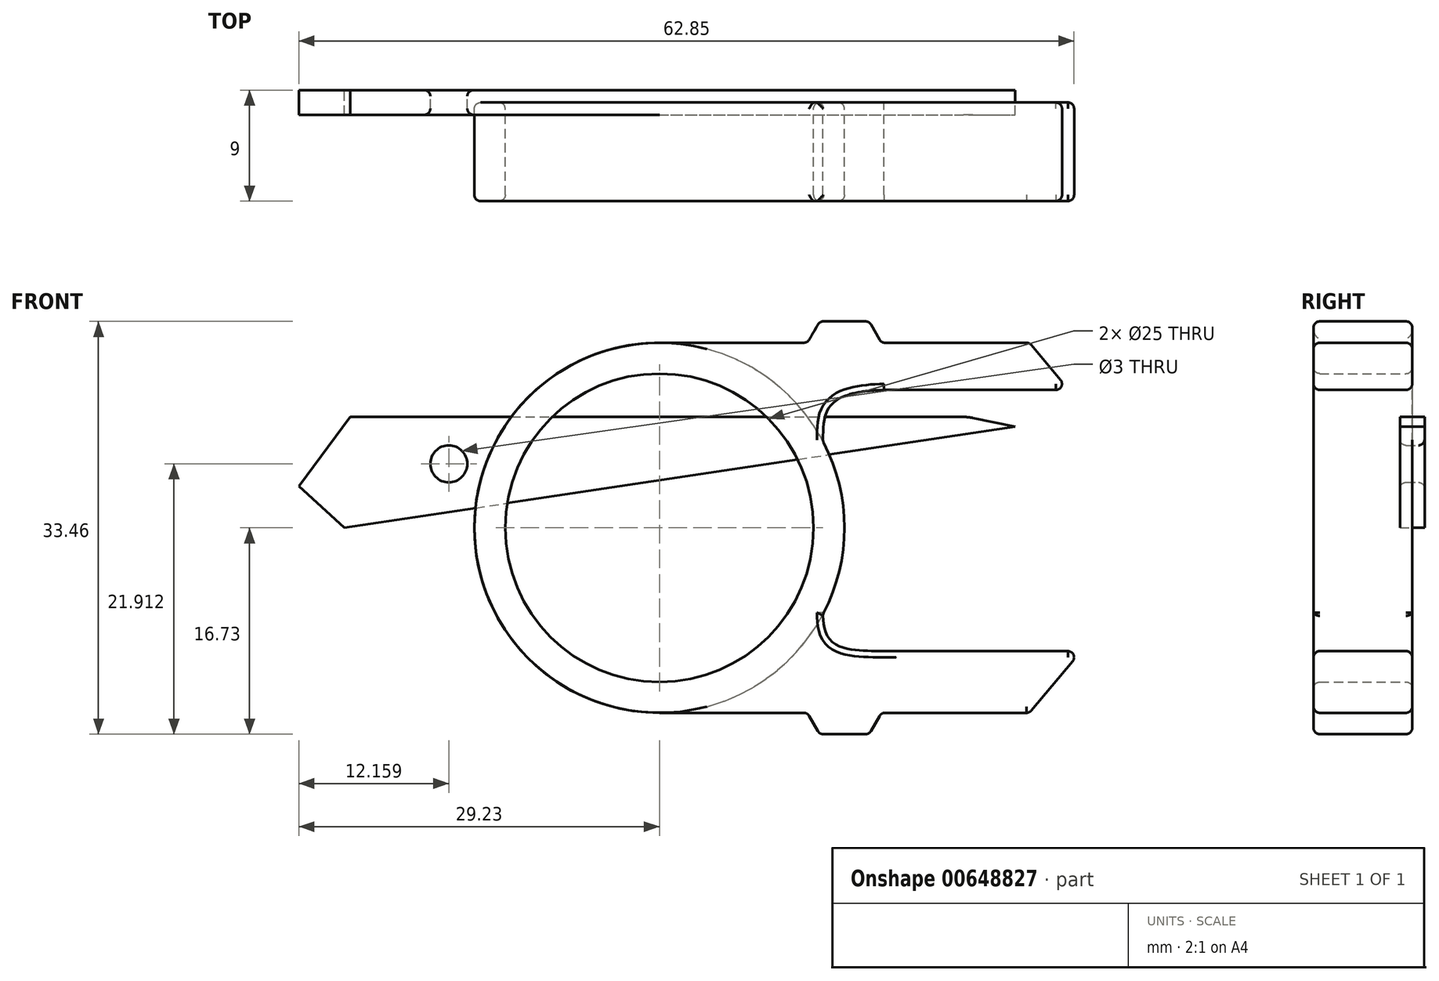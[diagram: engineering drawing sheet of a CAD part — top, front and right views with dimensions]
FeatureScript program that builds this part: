
annotation { "Feature Type Name" : "Feature", "Feature Type Description" : "" }
export const myFeature = defineFeature(function(context is Context, id is Id, definition is map)
    precondition{}
    {
        {
            var Q0;
            Q0=qCreatedBy(makeId("Front.planeOp"),FACE);
            var sketch = newSketch(context, id + "F0", { "sketchPlane" : qUnion([Q0])});
            skCircle(sketch, "E0", {"center": v(0, 0) * mm, "radius": 15 * mm});
            skCircle(sketch, "E1", {"center": v(0, 0) * mm, "radius": 12.5 * mm});
            skLineSegment(sketch, "E2", {"start": v(0, -15) * mm, "end": v(30, -15) * mm});
            skLineSegment(sketch, "E3", {"start": v(30, -15) * mm, "end": v(34.2, -10) * mm});
            skLineSegment(sketch, "E4", {"start": v(34.2, -10) * mm, "end": v(19.2, -10) * mm});
            skFitSpline(sketch, "E5", {"points": [v(19.2, -10) * mm, v(13.27, -7) * mm], "startDerivative": vector(-12.69, 0) * mm, "endDerivative": vector(0, 9) * mm});
            skLineSegment(sketch, "E6", {"start": v(12, -15) * mm, "end": v(13, -16.73) * mm});
            skLineSegment(sketch, "E7", {"start": v(13, -16.73) * mm, "end": v(17, -16.73) * mm});
            skLineSegment(sketch, "E8", {"start": v(17, -16.73) * mm, "end": v(18, -15) * mm});
            skSolve(sketch);
        }
        {
            var Q0;
            Q0=makeQuery(id+"F0.imprint","IMPRINT",FACE,{"disambiguationData":[TD([[makeQuery(id+"F0.imprint","IMPRINT",EDGE,{"derivedFrom":sQuery(id+"F0.wireOp",EDGE,"E1")}),-1.0]])]});
            var Q1;
            {var subQ5=sQuery(id+"F0.wireOp",EDGE,"E3");Q1=makeQuery(id+"F0.imprint","IMPRINT",FACE,{"disambiguationData":[TD([[makeQuery(id+"F0.imprint","IMPRINT",EDGE,{"derivedFrom":subQ5}),1.0]])]});}
            var Q2;
            {var subQ0=sQuery(id+"F0.wireOp",EDGE,"E6");Q2=makeQuery(id+"F0.imprint","IMPRINT",FACE,{"disambiguationData":[TD([[makeQuery(id+"F0.imprint","IMPRINT",EDGE,{"derivedFrom":subQ0}),1.0]])]});}
            extrude(context, id + "F1", {"entities" : qUnion([Q0, Q1, Q2]), "depth" : 8 * mm, "offsetDistance" : 25 * mm});
        }
        {
            var Q0;
            Q0=makeQuery(id+"F1.opExtrude","CAP_EDGE",EDGE,{"disambiguationData":[OSD([sQuery(id+"F0.wireOp",EDGE,"E1")])],"isStart":false});
            var Q1;
            Q1=makeQuery(id+"F1.opExtrude","CAP_EDGE",EDGE,{"disambiguationData":[OSD([sQuery(id+"F0.wireOp",EDGE,"E1")])],"isStart":true});
            fillet(context, id + "F2", {"entities" : qUnion([Q0, Q1]), "radius" : .5 * mm, "tangentPropagation" : true, "allowEdgeOverflow" : false});
        }
        {
            var Q0;
            Q0=makeQuery(id+"F1.opExtrude","CAP_EDGE",EDGE,{"disambiguationData":[OSD([sQuery(id+"F0.wireOp",EDGE,"E0")])],"isStart":false});
            var Q1;
            Q1=makeQuery(id+"F1.opExtrude","CAP_EDGE",EDGE,{"disambiguationData":[OSD([sQuery(id+"F0.wireOp",EDGE,"E0")])],"isStart":true});
            var Q2;
            Q2=makeQuery(id+"F1.opExtrude","CAP_EDGE",EDGE,{"disambiguationData":[OSD([sQuery(id+"F0.wireOp",EDGE,"E5")])],"isStart":false});
            var Q3;
            Q3=makeQuery(id+"F1.opExtrude","CAP_EDGE",EDGE,{"disambiguationData":[OSD([sQuery(id+"F0.wireOp",EDGE,"E5")])],"isStart":true});
            var Q4;
            Q4=makeQuery(id+"F1.opExtrude","CAP_EDGE",EDGE,{"disambiguationData":[OSD([sQuery(id+"F0.wireOp",EDGE,"E4")])],"isStart":true});
            var Q5;
            Q5=makeQuery(id+"F1.opExtrude","CAP_EDGE",EDGE,{"disambiguationData":[OSD([sQuery(id+"F0.wireOp",EDGE,"E4")])],"isStart":false});
            var Q6;
            {var subQ0=sQuery(id+"F0.wireOp",EDGE,"E2");Q6=makeQuery(id+"F1.opExtrude","CAP_EDGE",EDGE,{"disambiguationData":[OSD([subQ0]),TDD([makeQuery(id+"F0.imprint","IMPRINT",EDGE,{"disambiguationData":[TD([[makeQuery(id+"F0.imprint","INTERSECT",VERTEX,{"derivedFrom":[subQ0,sQuery(id+"F0.wireOp",EDGE,"E3")]}),1.0]])],"derivedFrom":subQ0})])],"isStart":false});}
            var Q7;
            {var subQ0=sQuery(id+"F0.wireOp",EDGE,"E2");Q7=makeQuery(id+"F1.opExtrude","CAP_EDGE",EDGE,{"disambiguationData":[OSD([subQ0]),TDD([makeQuery(id+"F0.imprint","IMPRINT",EDGE,{"disambiguationData":[TD([[makeQuery(id+"F0.imprint","INTERSECT",VERTEX,{"derivedFrom":[sQuery(id+"F0.wireOp",EDGE,"E0"),subQ0]}),-1.0]])],"derivedFrom":subQ0})])],"isStart":false});}
            fillet(context, id + "F3", {"entities" : qUnion([Q0, Q1, Q2, Q3, Q4, Q5, Q6, Q7]), "radius" : .5 * mm, "tangentPropagation" : true, "allowEdgeOverflow" : false});
        }
        {
            var Q0;
            Q0=makeQuery(id+"F1.opExtrude","CAP_EDGE",EDGE,{"disambiguationData":[OSD([sQuery(id+"F0.wireOp",EDGE,"E8")])],"isStart":false});
            var Q1;
            Q1=makeQuery(id+"F1.opExtrude","CAP_EDGE",EDGE,{"disambiguationData":[OSD([sQuery(id+"F0.wireOp",EDGE,"E7")])],"isStart":false});
            var Q2;
            Q2=makeQuery(id+"F1.opExtrude","CAP_EDGE",EDGE,{"disambiguationData":[OSD([sQuery(id+"F0.wireOp",EDGE,"E6")])],"isStart":false});
            var Q3;
            Q3=makeQuery(id+"F1.opExtrude","SWEPT_EDGE",EDGE,{"disambiguationData":[OSD([sQuery(id+"F0.wireOp",EDGE,"E6"),sQuery(id+"F0.wireOp",EDGE,"E7")])]});
            var Q4;
            Q4=makeQuery(id+"F1.opExtrude","SWEPT_EDGE",EDGE,{"disambiguationData":[OSD([sQuery(id+"F0.wireOp",EDGE,"E7"),sQuery(id+"F0.wireOp",EDGE,"E8")])]});
            var Q5;
            Q5=makeQuery(id+"F1.opExtrude","CAP_EDGE",EDGE,{"disambiguationData":[OSD([sQuery(id+"F0.wireOp",EDGE,"E6")])],"isStart":true});
            var Q6;
            Q6=makeQuery(id+"F1.opExtrude","CAP_EDGE",EDGE,{"disambiguationData":[OSD([sQuery(id+"F0.wireOp",EDGE,"E7")])],"isStart":true});
            var Q7;
            Q7=makeQuery(id+"F1.opExtrude","SWEPT_EDGE",EDGE,{"disambiguationData":[OSD([sQuery(id+"F0.wireOp",EDGE,"E2"),sQuery(id+"F0.wireOp",EDGE,"E6")])]});
            var Q8;
            Q8=makeQuery(id+"F1.opExtrude","SWEPT_EDGE",EDGE,{"disambiguationData":[OSD([sQuery(id+"F0.wireOp",EDGE,"E2"),sQuery(id+"F0.wireOp",EDGE,"E8")])]});
            var Q9;
            Q9=makeQuery(id+"F1.opExtrude","SWEPT_EDGE",EDGE,{"disambiguationData":[OSD([sQuery(id+"F0.wireOp",EDGE,"E2"),sQuery(id+"F0.wireOp",EDGE,"E3")])]});
            var Q10;
            Q10=makeQuery(id+"F1.opExtrude","SWEPT_EDGE",EDGE,{"disambiguationData":[OSD([sQuery(id+"F0.wireOp",EDGE,"E3"),sQuery(id+"F0.wireOp",EDGE,"E4")])]});
            var Q11;
            Q11=makeQuery(id+"F1.opExtrude","CAP_EDGE",EDGE,{"disambiguationData":[OSD([sQuery(id+"F0.wireOp",EDGE,"E8")])],"isStart":true});
            var Q12;
            {var subQ0=sQuery(id+"F0.wireOp",EDGE,"E2");Q12=makeQuery(id+"F1.opExtrude","CAP_EDGE",EDGE,{"disambiguationData":[OSD([subQ0]),TDD([makeQuery(id+"F0.imprint","IMPRINT",EDGE,{"disambiguationData":[TD([[makeQuery(id+"F0.imprint","INTERSECT",VERTEX,{"derivedFrom":[subQ0,sQuery(id+"F0.wireOp",EDGE,"E3")]}),1.0]])],"derivedFrom":subQ0})])],"isStart":true});}
            var Q13;
            {var subQ0=sQuery(id+"F0.wireOp",EDGE,"E2");var subQ1=makeQuery(id+"F0.imprint","IMPRINT",EDGE,{"disambiguationData":[TD([[makeQuery(id+"F0.imprint","INTERSECT",VERTEX,{"derivedFrom":[subQ0,sQuery(id+"F0.wireOp",EDGE,"E3")]}),1.0]])],"derivedFrom":subQ0});Q13=makeQuery(id+"F3.opFillet","BLEND_EDGE",EDGE,{"blendedFrom":[makeQuery(id+"F1.opExtrude","CAP_EDGE",EDGE,{"disambiguationData":[OSD([subQ0]),TDD([subQ1])],"isStart":false}),makeQuery(id+"F1.opExtrude","SWEPT_FACE",FACE,{"disambiguationData":[OSD([subQ0]),TDD([subQ1])]})],"blendedInto":[makeQuery(id+"F1.opExtrude","SWEPT_FACE",FACE,{"disambiguationData":[OSD([subQ0]),TDD([subQ1])]})]});}
            fillet(context, id + "F4", {"entities" : qUnion([Q0, Q1, Q2, Q3, Q4, Q5, Q6, Q7, Q8, Q9, Q10, Q11, Q12, Q13]), "radius" : .5 * mm, "tangentPropagation" : true, "allowEdgeOverflow" : false});
        }
        {
            var Q0;
            Q0=makeQuery(id+"F1.opExtrude","SWEPT_EDGE",EDGE,{"disambiguationData":[OSD([sQuery(id+"F0.wireOp",EDGE,"E0"),sQuery(id+"F0.wireOp",EDGE,"E5")])]});
            fillet(context, id + "F5", {"entities" : qUnion([Q0]), "radius" : .5 * mm, "tangentPropagation" : true, "allowEdgeOverflow" : false});
        }
        {
            var Q0;
            Q0=qCreatedBy(makeId("Front.planeOp"),FACE);
            var sketch = newSketch(context, id + "F6", { "sketchPlane" : qUnion([Q0])});
            skCircle(sketch, "E9", {"center": v(0, 0) * mm, "radius": 15 * mm});
            skCircle(sketch, "E10", {"center": v(0, 0) * mm, "radius": 12.5 * mm});
            skLineSegment(sketch, "E11", {"start": v(0, 15) * mm, "end": v(30, 15) * mm});
            skLineSegment(sketch, "E12", {"start": v(30, 15) * mm, "end": v(33.21, 11.17) * mm});
            skLineSegment(sketch, "E13", {"start": v(33.21, 11.17) * mm, "end": v(18.21, 11.17) * mm});
            skFitSpline(sketch, "E14", {"points": [v(18.21, 11.17) * mm, v(13.27, 7) * mm], "startDerivative": vector(-14.84, -0.37) * mm, "endDerivative": vector(0, -7.04) * mm});
            skLineSegment(sketch, "E15", {"start": v(12, 15) * mm, "end": v(13, 16.73) * mm});
            skLineSegment(sketch, "E16", {"start": v(13, 16.73) * mm, "end": v(17, 16.73) * mm});
            skLineSegment(sketch, "E17", {"start": v(17, 16.73) * mm, "end": v(18, 15) * mm});
            skSolve(sketch);
        }
        {
            var Q0;
            Q0=makeQuery(id+"F6.imprint","IMPRINT",FACE,{"disambiguationData":[TD([[makeQuery(id+"F6.imprint","IMPRINT",EDGE,{"derivedFrom":sQuery(id+"F6.wireOp",EDGE,"E10")}),-1.0]])]});
            var Q1;
            {var subQ5=sQuery(id+"F6.wireOp",EDGE,"E12");Q1=makeQuery(id+"F6.imprint","IMPRINT",FACE,{"disambiguationData":[TD([[makeQuery(id+"F6.imprint","IMPRINT",EDGE,{"derivedFrom":subQ5}),-1.0]])]});}
            var Q2;
            {var subQ0=sQuery(id+"F6.wireOp",EDGE,"E15");Q2=makeQuery(id+"F6.imprint","IMPRINT",FACE,{"disambiguationData":[TD([[makeQuery(id+"F6.imprint","IMPRINT",EDGE,{"derivedFrom":subQ0}),-1.0]])]});}
            extrude(context, id + "F7", {"entities" : qUnion([Q0, Q1, Q2]), "depth" : 8 * mm, "offsetDistance" : 25 * mm});
        }
        {
            var Q0;
            Q0=makeQuery(id+"F7.opExtrude","CAP_EDGE",EDGE,{"disambiguationData":[OSD([sQuery(id+"F6.wireOp",EDGE,"E9")])],"isStart":false});
            var Q1;
            Q1=makeQuery(id+"F7.opExtrude","CAP_EDGE",EDGE,{"disambiguationData":[OSD([sQuery(id+"F6.wireOp",EDGE,"E10")])],"isStart":false});
            var Q2;
            Q2=makeQuery(id+"F7.opExtrude","CAP_EDGE",EDGE,{"disambiguationData":[OSD([sQuery(id+"F6.wireOp",EDGE,"E10")])],"isStart":true});
            var Q3;
            {var subQ0=sQuery(id+"F6.wireOp",EDGE,"E11");Q3=makeQuery(id+"F7.opExtrude","CAP_EDGE",EDGE,{"disambiguationData":[OSD([subQ0]),TDD([makeQuery(id+"F6.imprint","IMPRINT",EDGE,{"disambiguationData":[TD([[makeQuery(id+"F6.imprint","INTERSECT",VERTEX,{"derivedFrom":[sQuery(id+"F6.wireOp",EDGE,"E9"),subQ0]}),-1.0]])],"derivedFrom":subQ0})])],"isStart":false});}
            var Q4;
            {var subQ0=sQuery(id+"F6.wireOp",EDGE,"E11");Q4=makeQuery(id+"F7.opExtrude","CAP_EDGE",EDGE,{"disambiguationData":[OSD([subQ0]),TDD([makeQuery(id+"F6.imprint","IMPRINT",EDGE,{"disambiguationData":[TD([[makeQuery(id+"F6.imprint","INTERSECT",VERTEX,{"derivedFrom":[sQuery(id+"F6.wireOp",EDGE,"E9"),subQ0]}),-1.0]])],"derivedFrom":subQ0})])],"isStart":true});}
            var Q5;
            Q5=makeQuery(id+"F7.opExtrude","CAP_EDGE",EDGE,{"disambiguationData":[OSD([sQuery(id+"F6.wireOp",EDGE,"E9")])],"isStart":true});
            var Q6;
            Q6=makeQuery(id+"F7.opExtrude","SWEPT_EDGE",EDGE,{"disambiguationData":[OSD([sQuery(id+"F6.wireOp",EDGE,"E15"),sQuery(id+"F6.wireOp",EDGE,"E16")])]});
            var Q7;
            Q7=makeQuery(id+"F7.opExtrude","SWEPT_EDGE",EDGE,{"disambiguationData":[OSD([sQuery(id+"F6.wireOp",EDGE,"E11"),sQuery(id+"F6.wireOp",EDGE,"E15")])]});
            var Q8;
            Q8=makeQuery(id+"F7.opExtrude","SWEPT_EDGE",EDGE,{"disambiguationData":[OSD([sQuery(id+"F6.wireOp",EDGE,"E16"),sQuery(id+"F6.wireOp",EDGE,"E17")])]});
            var Q9;
            Q9=makeQuery(id+"F7.opExtrude","CAP_EDGE",EDGE,{"disambiguationData":[OSD([sQuery(id+"F6.wireOp",EDGE,"E17")])],"isStart":false});
            var Q10;
            Q10=makeQuery(id+"F7.opExtrude","SWEPT_EDGE",EDGE,{"disambiguationData":[OSD([sQuery(id+"F6.wireOp",EDGE,"E11"),sQuery(id+"F6.wireOp",EDGE,"E17")])]});
            var Q11;
            Q11=makeQuery(id+"F7.opExtrude","CAP_EDGE",EDGE,{"disambiguationData":[OSD([sQuery(id+"F6.wireOp",EDGE,"E17")])],"isStart":true});
            var Q12;
            Q12=makeQuery(id+"F7.opExtrude","SWEPT_EDGE",EDGE,{"disambiguationData":[OSD([sQuery(id+"F6.wireOp",EDGE,"E11"),sQuery(id+"F6.wireOp",EDGE,"E12")])]});
            var Q13;
            Q13=makeQuery(id+"F7.opExtrude","CAP_EDGE",EDGE,{"disambiguationData":[OSD([sQuery(id+"F6.wireOp",EDGE,"E13")])],"isStart":true});
            var Q14;
            Q14=makeQuery(id+"F7.opExtrude","CAP_EDGE",EDGE,{"disambiguationData":[OSD([sQuery(id+"F6.wireOp",EDGE,"E13")])],"isStart":false});
            var Q15;
            Q15=makeQuery(id+"F7.opExtrude","SWEPT_EDGE",EDGE,{"disambiguationData":[OSD([sQuery(id+"F6.wireOp",EDGE,"E9"),sQuery(id+"F6.wireOp",EDGE,"E14")])]});
            var Q16;
            Q16=makeQuery(id+"F7.opExtrude","CAP_EDGE",EDGE,{"disambiguationData":[OSD([sQuery(id+"F6.wireOp",EDGE,"E16")])],"isStart":true});
            var Q17;
            Q17=makeQuery(id+"F7.opExtrude","CAP_EDGE",EDGE,{"disambiguationData":[OSD([sQuery(id+"F6.wireOp",EDGE,"E16")])],"isStart":false});
            fillet(context, id + "F8", {"entities" : qUnion([Q0, Q1, Q2, Q3, Q4, Q5, Q6, Q7, Q8, Q9, Q10, Q11, Q12, Q13, Q14, Q15, Q16, Q17]), "radius" : .5 * mm, "tangentPropagation" : true, "allowEdgeOverflow" : false});
        }
        {
            var Q0;
            Q0=makeQuery(id+"F7.opExtrude","CAP_EDGE",EDGE,{"disambiguationData":[OSD([sQuery(id+"F6.wireOp",EDGE,"E12")])],"isStart":true});
            var Q1;
            Q1=makeQuery(id+"F7.opExtrude","CAP_EDGE",EDGE,{"disambiguationData":[OSD([sQuery(id+"F6.wireOp",EDGE,"E12")])],"isStart":false});
            var Q2;
            Q2=makeQuery(id+"F7.opExtrude","SWEPT_EDGE",EDGE,{"disambiguationData":[OSD([sQuery(id+"F6.wireOp",EDGE,"E12"),sQuery(id+"F6.wireOp",EDGE,"E13")])]});
            fillet(context, id + "F9", {"entities" : qUnion([Q0, Q1, Q2]), "radius" : .5 * mm, "tangentPropagation" : true, "allowEdgeOverflow" : false});
        }
        {
            var Q0;
            Q0=qCreatedBy(makeId("Front.planeOp"),FACE);
            var sketch = newSketch(context, id + "F10", { "sketchPlane" : qUnion([Q0])});
            skLineSegment(sketch, "E18", {"start": v(-25.07, 9) * mm, "end": v(24.93, 9) * mm});
            skLineSegment(sketch, "E19", {"start": v(-25.07, 9) * mm, "end": v(-29.23, 3.37) * mm});
            skLineSegment(sketch, "E20", {"start": v(-29.23, 3.37) * mm, "end": v(-25.53, 0) * mm});
            skLineSegment(sketch, "E21", {"start": v(-25.53, 0) * mm, "end": v(28.85, 8.2) * mm});
            skLineSegment(sketch, "E22", {"start": v(24.93, 9) * mm, "end": v(28.85, 8.2) * mm});
            skLineSegment(sketch, "E23", {"start": v(-25.07, 9) * mm, "end": v(-25.07, 5.18) * mm, "construction": true});
            skLineSegment(sketch, "E24", {"start": v(-25.07, 5.18) * mm, "end": v(-17.07, 5.18) * mm, "construction": true});
            skLineSegment(sketch, "E25", {"start": v(-17.07, 9) * mm, "end": v(-17.07, 5.18) * mm, "construction": true});
            skPoint(sketch, "E26", {"position": v(-17.07, 5.18) * mm});
            skCircle(sketch, "E27", {"center": v(-17.07, 5.18) * mm, "radius": 1.5 * mm});
            skLineSegment(sketch, "E28", {"start": v(-17.34, 21.21) * mm, "end": v(0, 20.3) * mm});
            skSolve(sketch);
        }
        {
            var Q0;
            Q0=makeQuery(id+"F10.imprint","IMPRINT",FACE,{"disambiguationData":[TD([[makeQuery(id+"F10.imprint","IMPRINT",EDGE,{"derivedFrom":sQuery(id+"F10.wireOp",EDGE,"E18")}),-1.0]])]});
            extrude(context, id + "F11", {"entities" : qUnion([Q0]), "endBound" : BoundingType.SYMMETRIC, "depth" : 2 * mm, "offsetDistance" : 25 * mm});
        }
        {
            var Q0;
            Q0=makeQuery(id+"F11.opExtrude","SWEPT_EDGE",EDGE,{"disambiguationData":[OSD([sQuery(id+"F10.wireOp",EDGE,"E18"),sQuery(id+"F10.wireOp",EDGE,"E22")])]});
            fillet(context, id + "F12", {"entities" : qUnion([Q0]), "radius" : 5 * mm, "tangentPropagation" : true, "allowEdgeOverflow" : false});
        }
        {
            var Q0;
            Q0=makeQuery(id+"F11.opExtrude","CAP_EDGE",EDGE,{"disambiguationData":[OSD([sQuery(id+"F10.wireOp",EDGE,"E27")])],"isStart":false});
            var Q1;
            Q1=makeQuery(id+"F11.opExtrude","CAP_EDGE",EDGE,{"disambiguationData":[OSD([sQuery(id+"F10.wireOp",EDGE,"E27")])],"isStart":true});
            fillet(context, id + "F13", {"entities" : qUnion([Q0, Q1]), "radius" : .5 * mm, "tangentPropagation" : true, "allowEdgeOverflow" : false});
        }
    });
